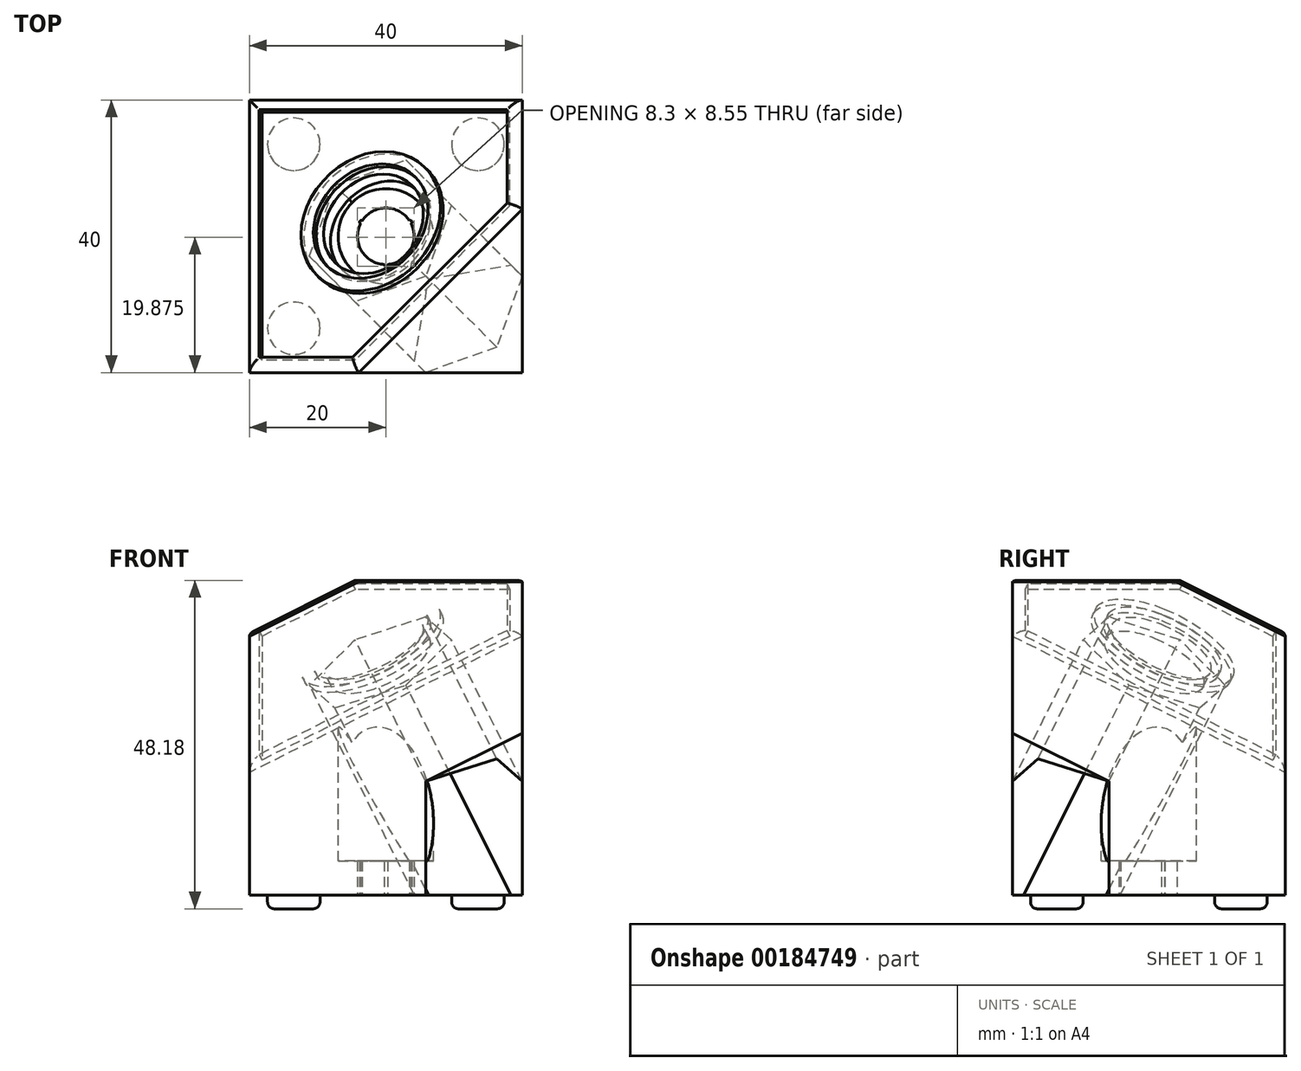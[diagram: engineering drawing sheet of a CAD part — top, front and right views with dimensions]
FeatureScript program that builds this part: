
annotation { "Feature Type Name" : "Feature", "Feature Type Description" : "" }
export const myFeature = defineFeature(function(context is Context, id is Id, definition is map)
    precondition{}
    {
        {
            var Q0;
            Q0=qCreatedBy(makeId("Top.planeOp"),FACE);
            var sketch = newSketch(context, id + "F0", { "sketchPlane" : qUnion([Q0])});
            skLineSegment(sketch, "E0.bottom", {"start": v(20, -20) * mm, "end": v(-20, -20) * mm});
            skLineSegment(sketch, "E0.top", {"start": v(20, 20) * mm, "end": v(-20, 20) * mm});
            skLineSegment(sketch, "E0.left", {"start": v(20, -20) * mm, "end": v(20, 20) * mm});
            skLineSegment(sketch, "E0.right", {"start": v(-20, -20) * mm, "end": v(-20, 20) * mm});
            skPoint(sketch, "E0.middle", {"position": v(0, 0) * mm});
            skSolve(sketch);
        }
        {
            var Q0;
            Q0=makeQuery(id+"F0.imprint","IMPRINT",FACE,{"disambiguationData":[TD([[makeQuery(id+"F0.imprint","IMPRINT",EDGE,{"derivedFrom":sQuery(id+"F0.wireOp",EDGE,"E0.bottom")}),-1.0]])]});
            extrude(context, id + "F1", {"entities" : qUnion([Q0]), "depth" : 20 * mm});
        }
        {
            var Q0;
            Q0=makeQuery(id+"F1.opExtrude","CAP_VERTEX",VERTEX,{"disambiguationData":[OSD([sQuery(id+"F0.wireOp",EDGE,"E0.top"),sQuery(id+"F0.wireOp",EDGE,"E0.left")])],"isStart":false});
            var Q1;
            Q1=makeQuery(id+"F1.opExtrude","CAP_VERTEX",VERTEX,{"disambiguationData":[OSD([sQuery(id+"F0.wireOp",EDGE,"E0.bottom"),sQuery(id+"F0.wireOp",EDGE,"E0.right")])],"isStart":false});
            var Q2;
            Q2=makeQuery(id+"F1.opExtrude","CAP_VERTEX",VERTEX,{"disambiguationData":[OSD([sQuery(id+"F0.wireOp",EDGE,"E0.top"),sQuery(id+"F0.wireOp",EDGE,"E0.right")])],"isStart":true});
            cPlane(context, id + "F2", {"entities" : qUnion([Q0, Q1, Q2]), "cplaneType" : CPlaneType.THREE_POINT, "offset" : 25 * mm, "width" : 150 * mm, "height" : 150 * mm});
        }
        {
            var Q0;
            Q0=makeQuery(id+"F1.opExtrude","CAP_FACE",FACE,{"disambiguationData":[OSD([sQuery(id+"F0.wireOp",EDGE,"E0.bottom"),sQuery(id+"F0.wireOp",EDGE,"E0.top"),sQuery(id+"F0.wireOp",EDGE,"E0.left"),sQuery(id+"F0.wireOp",EDGE,"E0.right")])],"isStart":true});
            extrude(context, id + "F3", {"entities" : qUnion([Q0]), "operationType" : NewBodyOperationType.ADD, "depth" : 18 * mm});
        }
        {
            var Q0;
            Q0=makeQuery(id+"F1.opExtrude","CAP_FACE",FACE,{"disambiguationData":[OSD([sQuery(id+"F0.wireOp",EDGE,"E0.bottom"),sQuery(id+"F0.wireOp",EDGE,"E0.top"),sQuery(id+"F0.wireOp",EDGE,"E0.left"),sQuery(id+"F0.wireOp",EDGE,"E0.right")])],"isStart":false});
            extrude(context, id + "F4", {"entities" : qUnion([Q0]), "operationType" : NewBodyOperationType.ADD, "depth" : 8 * mm});
        }
        {
            var Q0;
            Q0=qCreatedBy(id+"F2.planeOp",FACE);
            var sketch = newSketch(context, id + "F5", { "sketchPlane" : qUnion([Q0])});
            skCircle(sketch, "E1", {"center": v(2.39, -7.49) * mm, "radius": 48.4 * mm});
            skSolve(sketch);
        }
        {
            var Q0;
            Q0=makeQuery(id+"F5.imprint","IMPRINT",FACE,{"disambiguationData":[TD([[makeQuery(id+"F5.imprint","IMPRINT",EDGE,{"derivedFrom":sQuery(id+"F5.wireOp",EDGE,"E1")}),1.0]])]});
            extrude(context, id + "F6", {"entities" : qUnion([Q0]), "operationType" : NewBodyOperationType.REMOVE, "depth" : 25 * mm});
        }
        {
            var Q0;
            Q0=makeQuery(id+"F6.boolean.opBoolean","COPY",FACE,{"derivedFrom":makeQuery(id+"F6.opExtrude","CAP_FACE",FACE,{"disambiguationData":[OSD([sQuery(id+"F5.wireOp",EDGE,"E1")])],"isStart":true})});
            var sketch = newSketch(context, id + "F7", { "sketchPlane" : qUnion([Q0])});
            skLineSegment(sketch, "E2", {"start": v(16.07, -19.68) * mm, "end": v(-14.6, 17.89) * mm, "construction": true});
            skCircle(sketch, "E3", {"center": v(5.31, -6.5) * mm, "radius": 8 * mm});
            skSolve(sketch);
        }
        {
            var Q0;
            Q0=makeQuery(id+"F7.imprint","IMPRINT",FACE,{"disambiguationData":[TD([[makeQuery(id+"F7.imprint","IMPRINT",EDGE,{"derivedFrom":sQuery(id+"F7.wireOp",EDGE,"E3")}),1.0]])]});
            extrude(context, id + "F8", {"entities" : qUnion([Q0]), "operationType" : NewBodyOperationType.REMOVE, "endBound" : BoundingType.THROUGH_ALL, "oppositeDirection" : true, "depth" : 25 * mm});
        }
        {
            var Q0;
            Q0=qCreatedBy(id+"F2.planeOp",FACE);
            cPlane(context, id + "F9", {"entities" : qUnion([Q0]), "cplaneType" : CPlaneType.OFFSET, "offset" : 40 * mm, "oppositeDirection" : true, "width" : 150 * mm, "height" : 150 * mm});
        }
        {
            var Q0;
            Q0=qCreatedBy(id+"F9.planeOp",FACE);
            var sketch = newSketch(context, id + "F10", { "sketchPlane" : qUnion([Q0])});
            skArc(sketch, "E4.0", {"start": v(10.03, -0.05) * mm, "mid": v(0.26, -0.31) * mm, "end": v(-1.96, -9.84) * mm, "construction": true});
            skArc(sketch, "E5.0", {"start": v(10.37, -12.7) * mm, "mid": v(3.5, -14.3) * mm, "end": v(-1.96, -9.84) * mm, "construction": true});
            skArc(sketch, "E6.0", {"start": v(10.37, -12.7) * mm, "mid": v(13.31, -6.3) * mm, "end": v(10.03, -0.05) * mm, "construction": true});
            skCircle(sketch, "E7.cCircle", {"center": v(5.31, -6.5) * mm, "radius": 10 * mm, "construction": true});
            skLineSegment(sketch, "E7.0", {"start": v(9.4, 4.29) * mm, "end": v(16.71, -4.66) * mm});
            skLineSegment(sketch, "E7.1", {"start": v(16.71, -4.66) * mm, "end": v(12.62, -15.45) * mm});
            skLineSegment(sketch, "E7.2", {"start": v(12.62, -15.45) * mm, "end": v(1.22, -17.3) * mm});
            skLineSegment(sketch, "E7.3", {"start": v(1.22, -17.3) * mm, "end": v(-6.08, -8.36) * mm});
            skLineSegment(sketch, "E7.4", {"start": v(-6.08, -8.36) * mm, "end": v(-1.99, 2.44) * mm});
            skLineSegment(sketch, "E7.5", {"start": v(-1.99, 2.44) * mm, "end": v(9.4, 4.29) * mm});
            skPoint(sketch, "E7.0.midPoint", {"position": v(13.06, -0.18) * mm});
            skLineSegment(sketch, "E8.0", {"start": v(24.83, -30.41) * mm, "end": v(10.37, -12.7) * mm, "construction": true});
            skLineSegment(sketch, "E9", {"start": v(-18.46, -33.37) * mm, "end": v(44.1, 17.7) * mm});
            skLineSegment(sketch, "E10", {"start": v(44.1, 17.7) * mm, "end": v(61.04, -3.05) * mm});
            skLineSegment(sketch, "E11", {"start": v(61.04, -3.05) * mm, "end": v(-1.51, -54.13) * mm});
            skLineSegment(sketch, "E12", {"start": v(-1.51, -54.13) * mm, "end": v(-18.46, -33.37) * mm});
            skSolve(sketch);
        }
        {
            var Q0;
            Q0=makeQuery(id+"F10.imprint","IMPRINT",FACE,{"disambiguationData":[TD([[makeQuery(id+"F10.imprint","IMPRINT",EDGE,{"derivedFrom":sQuery(id+"F10.wireOp",EDGE,"E7.0")}),-1.0]])]});
            var Q1;
            {var subQ0=sQuery(id+"F10.wireOp",EDGE,"E7.2");Q1=makeQuery(id+"F10.imprint","IMPRINT",FACE,{"disambiguationData":[TD([[makeQuery(id+"F10.imprint","IMPRINT",EDGE,{"derivedFrom":subQ0}),-1.0]])]});}
            extrude(context, id + "F11", {"entities" : qUnion([Q0, Q1]), "operationType" : NewBodyOperationType.REMOVE, "endBound" : BoundingType.SYMMETRIC, "oppositeDirection" : true, "depth" : 75 * mm});
        }
        {
            var Q0;
            {var subQ1=sQuery(id+"F10.wireOp",EDGE,"E7.1");Q0=makeQuery(id+"F10.imprint","IMPRINT",FACE,{"disambiguationData":[TD([[makeQuery(id+"F10.imprint","IMPRINT",EDGE,{"derivedFrom":subQ1}),1.0]])]});}
            extrude(context, id + "F12", {"entities" : qUnion([Q0]), "operationType" : NewBodyOperationType.REMOVE, "depth" : 12.05 * mm});
        }
        {
            var Q0;
            Q0=makeQuery(id+"F3.opExtrude","CAP_FACE",FACE,{"disambiguationData":[OSD([sQuery(id+"F0.wireOp",EDGE,"E0.bottom"),sQuery(id+"F0.wireOp",EDGE,"E0.top"),sQuery(id+"F0.wireOp",EDGE,"E0.left"),sQuery(id+"F0.wireOp",EDGE,"E0.right")])],"isStart":false});
            var sketch = newSketch(context, id + "F13", { "sketchPlane" : qUnion([Q0])});
            skArc(sketch, "E13", {"start": v(-0.25, 4.14) * mm, "mid": v(-3.6, 2.08) * mm, "end": v(-3.71, -1.85) * mm});
            skArc(sketch, "E14", {"start": v(0.25, 4.14) * mm, "mid": v(0, 4.4) * mm, "end": v(-0.25, 4.14) * mm});
            skArc(sketch, "E15.1.0", {"start": v(-3.71, -1.85) * mm, "mid": v(-3.81, -2.2) * mm, "end": v(-3.46, -2.29) * mm});
            skArc(sketch, "E15.2.0", {"start": v(3.46, -2.29) * mm, "mid": v(3.81, -2.2) * mm, "end": v(3.71, -1.85) * mm});
            skArc(sketch, "E16.trimOffspring", {"start": v(3.71, -1.85) * mm, "mid": v(3.6, 2.08) * mm, "end": v(0.25, 4.14) * mm});
            skArc(sketch, "E17.trimOffspring", {"start": v(-3.46, -2.29) * mm, "mid": v(0, -4.15) * mm, "end": v(3.46, -2.29) * mm});
            skCircle(sketch, "E18", {"center": v(-13.5, 13.5) * mm, "radius": 3.85 * mm});
            skCircle(sketch, "E19.1.0", {"center": v(-13.5, -13.5) * mm, "radius": 3.85 * mm});
            skCircle(sketch, "E19.2.0", {"center": v(13.5, -13.5) * mm, "radius": 3.85 * mm});
            skCircle(sketch, "E19.3.0", {"center": v(13.5, 13.5) * mm, "radius": 3.85 * mm});
            skLineSegment(sketch, "E20.rect.bottom", {"start": v(19, -20) * mm, "end": v(-19, -20) * mm});
            skLineSegment(sketch, "E20.rect.top", {"start": v(19, 20) * mm, "end": v(4.2, 20) * mm});
            skLineSegment(sketch, "E20.rect.left", {"start": v(20, -19) * mm, "end": v(20, 19) * mm});
            skLineSegment(sketch, "E20.rect.right", {"start": v(-20, -19) * mm, "end": v(-20, 19) * mm});
            skPoint(sketch, "E21.visualSharp", {"position": v(-20, 20) * mm});
            skArc(sketch, "E21.filletArc", {"start": v(-19, 20) * mm, "mid": v(-19.7, 19.7) * mm, "end": v(-20, 19) * mm});
            skPoint(sketch, "E22.visualSharp", {"position": v(20, 20) * mm});
            skArc(sketch, "E22.filletArc", {"start": v(20, 19) * mm, "mid": v(19.7, 19.7) * mm, "end": v(19, 20) * mm});
            skPoint(sketch, "E23.visualSharp", {"position": v(-20, -20) * mm});
            skArc(sketch, "E23.filletArc", {"start": v(-20, -19) * mm, "mid": v(-19.7, -19.7) * mm, "end": v(-19, -20) * mm});
            skPoint(sketch, "E24.visualSharp", {"position": v(20, -20) * mm});
            skArc(sketch, "E24.filletArc", {"start": v(19, -20) * mm, "mid": v(19.7, -19.7) * mm, "end": v(20, -19) * mm});
            skLineSegment(sketch, "E25.rect.bottom", {"start": v(-16, -4.2) * mm, "end": v(-20, -4.2) * mm});
            skLineSegment(sketch, "E25.rect.top", {"start": v(-16, 4.2) * mm, "end": v(-20, 4.2) * mm});
            skLineSegment(sketch, "E25.rect.right", {"start": v(-20, -4.2) * mm, "end": v(-20, 4.2) * mm});
            skPoint(sketch, "E25.rect.middle", {"position": v(-18, 0) * mm});
            skLineSegment(sketch, "E26.rect.bottom", {"start": v(-16, 7.25) * mm, "end": v(-9.36, 7.25) * mm});
            skLineSegment(sketch, "E26.rect.top", {"start": v(-16, -7.25) * mm, "end": v(-9.36, -7.25) * mm});
            skLineSegment(sketch, "E26.rect.left", {"start": v(-16, 7.25) * mm, "end": v(-16, 4.2) * mm});
            skPoint(sketch, "E26.rect.middle", {"position": v(-12.68, 0) * mm});
            skPoint(sketch, "E26.rect.middle.positionSnap0", {"position": v(-16, 0) * mm});
            skPoint(sketch, "E26.rect.cornerSnap0", {"position": v(-16, 0) * mm});
            skPoint(sketch, "E26.rect.centerSnap0", {"position": v(-16, 0) * mm});
            skLineSegment(sketch, "E27.trimOffspring", {"start": v(-16, -4.2) * mm, "end": v(-16, -7.25) * mm});
            skArc(sketch, "E28", {"start": v(-9.36, 7.25) * mm, "mid": v(-6, 0) * mm, "end": v(-9.36, -7.25) * mm});
            skLineSegment(sketch, "E29.1.0", {"start": v(4.2, -16) * mm, "end": v(7.25, -16) * mm});
            skLineSegment(sketch, "E29.1.1", {"start": v(4.2, -16) * mm, "end": v(4.2, -20) * mm});
            skPoint(sketch, "E29.1.2", {"position": v(0, -16) * mm});
            skLineSegment(sketch, "E29.1.3", {"start": v(-7.25, -16) * mm, "end": v(-4.2, -16) * mm});
            skPoint(sketch, "E29.1.4", {"position": v(0, -18) * mm});
            skLineSegment(sketch, "E29.1.5", {"start": v(7.25, -16) * mm, "end": v(7.25, -9.36) * mm});
            skArc(sketch, "E29.1.6", {"start": v(-7.25, -9.36) * mm, "mid": v(0, -6) * mm, "end": v(7.25, -9.36) * mm});
            skLineSegment(sketch, "E29.1.7", {"start": v(-7.25, -16) * mm, "end": v(-7.25, -9.36) * mm});
            skLineSegment(sketch, "E29.1.8", {"start": v(4.2, -20) * mm, "end": v(-4.2, -20) * mm});
            skLineSegment(sketch, "E29.1.9", {"start": v(-4.2, -16) * mm, "end": v(-4.2, -20) * mm});
            skPoint(sketch, "E29.1.10", {"position": v(0, -12.68) * mm});
            skPoint(sketch, "E29.1.11", {"position": v(0, -16) * mm});
            skPoint(sketch, "E29.1.12", {"position": v(0, -16) * mm});
            skLineSegment(sketch, "E29.2.0", {"start": v(16, 4.2) * mm, "end": v(16, 7.25) * mm});
            skLineSegment(sketch, "E29.2.1", {"start": v(16, 4.2) * mm, "end": v(20, 4.2) * mm});
            skPoint(sketch, "E29.2.2", {"position": v(16, 0) * mm});
            skLineSegment(sketch, "E29.2.3", {"start": v(16, -7.25) * mm, "end": v(16, -4.2) * mm});
            skPoint(sketch, "E29.2.4", {"position": v(18, 0) * mm});
            skLineSegment(sketch, "E29.2.5", {"start": v(16, 7.25) * mm, "end": v(9.36, 7.25) * mm});
            skArc(sketch, "E29.2.6", {"start": v(9.36, -7.25) * mm, "mid": v(6, 0) * mm, "end": v(9.36, 7.25) * mm});
            skLineSegment(sketch, "E29.2.7", {"start": v(16, -7.25) * mm, "end": v(9.36, -7.25) * mm});
            skLineSegment(sketch, "E29.2.8", {"start": v(20, 4.2) * mm, "end": v(20, -4.2) * mm});
            skLineSegment(sketch, "E29.2.9", {"start": v(16, -4.2) * mm, "end": v(20, -4.2) * mm});
            skPoint(sketch, "E29.2.10", {"position": v(12.68, 0) * mm});
            skPoint(sketch, "E29.2.11", {"position": v(16, 0) * mm});
            skPoint(sketch, "E29.2.12", {"position": v(16, 0) * mm});
            skLineSegment(sketch, "E29.3.0", {"start": v(-4.2, 16) * mm, "end": v(-7.25, 16) * mm});
            skLineSegment(sketch, "E29.3.1", {"start": v(-4.2, 16) * mm, "end": v(-4.2, 20) * mm});
            skPoint(sketch, "E29.3.2", {"position": v(0, 16) * mm});
            skLineSegment(sketch, "E29.3.3", {"start": v(7.25, 16) * mm, "end": v(4.2, 16) * mm});
            skPoint(sketch, "E29.3.4", {"position": v(0, 18) * mm});
            skLineSegment(sketch, "E29.3.5", {"start": v(-7.25, 16) * mm, "end": v(-7.25, 9.36) * mm});
            skArc(sketch, "E29.3.6", {"start": v(7.25, 9.36) * mm, "mid": v(0, 6) * mm, "end": v(-7.25, 9.36) * mm});
            skLineSegment(sketch, "E29.3.7", {"start": v(7.25, 16) * mm, "end": v(7.25, 9.36) * mm});
            skLineSegment(sketch, "E29.3.8", {"start": v(-4.2, 20) * mm, "end": v(4.2, 20) * mm});
            skLineSegment(sketch, "E29.3.9", {"start": v(4.2, 16) * mm, "end": v(4.2, 20) * mm});
            skPoint(sketch, "E29.3.10", {"position": v(0, 12.68) * mm});
            skPoint(sketch, "E29.3.11", {"position": v(0, 16) * mm});
            skPoint(sketch, "E29.3.12", {"position": v(0, 16) * mm});
            skLineSegment(sketch, "E30.trimOffspring", {"start": v(-4.2, 20) * mm, "end": v(-19, 20) * mm});
            skSolve(sketch);
        }
        {
            var Q0;
            Q0=makeQuery(id+"F13.imprint","IMPRINT",FACE,{"disambiguationData":[TD([[makeQuery(id+"F13.imprint","IMPRINT",EDGE,{"derivedFrom":sQuery(id+"F13.wireOp",EDGE,"E18")}),1.0]])]});
            var Q1;
            Q1=makeQuery(id+"F13.imprint","IMPRINT",FACE,{"disambiguationData":[TD([[makeQuery(id+"F13.imprint","IMPRINT",EDGE,{"derivedFrom":sQuery(id+"F13.wireOp",EDGE,"E19.1.0")}),1.0]])]});
            var Q2;
            Q2=makeQuery(id+"F13.imprint","IMPRINT",FACE,{"disambiguationData":[TD([[makeQuery(id+"F13.imprint","IMPRINT",EDGE,{"derivedFrom":sQuery(id+"F13.wireOp",EDGE,"E19.2.0")}),1.0]])]});
            extrude(context, id + "F14", {"entities" : qUnion([Q0, Q1, Q2]), "operationType" : NewBodyOperationType.ADD, "depth" : 2 * mm});
        }
        {
            var Q0;
            Q0=makeQuery(id+"F13.imprint","IMPRINT",FACE,{"disambiguationData":[TD([[makeQuery(id+"F13.imprint","IMPRINT",EDGE,{"derivedFrom":sQuery(id+"F13.wireOp",EDGE,"E13")}),1.0]])]});
            extrude(context, id + "F15", {"entities" : qUnion([Q0]), "operationType" : NewBodyOperationType.REMOVE, "oppositeDirection" : true, "depth" : 25 * mm});
        }
        {
            var Q0;
            Q0=qCreatedBy(makeId("Top.planeOp"),FACE);
            var sketch = newSketch(context, id + "F16", { "sketchPlane" : qUnion([Q0])});
            skCircle(sketch, "E31", {"center": v(0, 0) * mm, "radius": 7 * mm});
            skSolve(sketch);
        }
        {
            var Q0;
            Q0=makeQuery(id+"F16.imprint","IMPRINT",FACE,{"disambiguationData":[TD([[makeQuery(id+"F16.imprint","IMPRINT",EDGE,{"derivedFrom":sQuery(id+"F16.wireOp",EDGE,"E31")}),1.0]])]});
            extrude(context, id + "F17", {"entities" : qUnion([Q0]), "operationType" : NewBodyOperationType.REMOVE, "oppositeDirection" : true, "depth" : 13 * mm});
        }
        {
            var Q0;
            Q0=makeQuery(id+"F16.imprint","IMPRINT",FACE,{"disambiguationData":[TD([[makeQuery(id+"F16.imprint","IMPRINT",EDGE,{"derivedFrom":sQuery(id+"F16.wireOp",EDGE,"E31")}),1.0]])]});
            extrude(context, id + "F18", {"entities" : qUnion([Q0]), "operationType" : NewBodyOperationType.REMOVE, "depth" : 18.5 * mm});
        }
        {
            var Q0;
            Q0=makeQuery(id+"F14.opExtrude","CAP_EDGE",EDGE,{"disambiguationData":[OSD([sQuery(id+"F13.wireOp",EDGE,"E19.1.0")])],"isStart":false});
            var Q1;
            Q1=makeQuery(id+"F14.opExtrude","CAP_EDGE",EDGE,{"disambiguationData":[OSD([sQuery(id+"F13.wireOp",EDGE,"E18")])],"isStart":false});
            var Q2;
            Q2=makeQuery(id+"F14.opExtrude","CAP_EDGE",EDGE,{"disambiguationData":[OSD([sQuery(id+"F13.wireOp",EDGE,"E19.2.0")])],"isStart":false});
            fillet(context, id + "F19", {"entities" : qUnion([Q0, Q1, Q2]), "radius" : 1 * mm, "tangentPropagation" : true, "allowEdgeOverflow" : false});
        }
        {
            var Q0;
            Q0=makeQuery(id+"F6.boolean.opBoolean","COPY",FACE,{"derivedFrom":makeQuery(id+"F6.opExtrude","CAP_FACE",FACE,{"disambiguationData":[OSD([sQuery(id+"F5.wireOp",EDGE,"E1")])],"isStart":true})});
            var sketch = newSketch(context, id + "F20", { "sketchPlane" : qUnion([Q0])});
            skLineSegment(sketch, "E32.0", {"start": v(29.21, -8.94) * mm, "end": v(29.21, 8.94) * mm});
            skLineSegment(sketch, "E33.0", {"start": v(29.21, -8.94) * mm, "end": v(2.92, -30.41) * mm});
            skLineSegment(sketch, "E34.0", {"start": v(2.92, -30.41) * mm, "end": v(-14.6, -26.83) * mm});
            skLineSegment(sketch, "E35.0", {"start": v(-14.6, -26.83) * mm, "end": v(-14.6, 17.89) * mm});
            skLineSegment(sketch, "E36.0", {"start": v(29.21, 8.94) * mm, "end": v(-14.6, 17.89) * mm});
            skLineSegment(sketch, "E37.0", {"start": v(2.4, -28.26) * mm, "end": v(-12.6, -25.2) * mm});
            skLineSegment(sketch, "E37.1", {"start": v(27.21, -8) * mm, "end": v(2.4, -28.26) * mm});
            skLineSegment(sketch, "E37.2", {"start": v(-12.6, -25.2) * mm, "end": v(-12.6, 15.44) * mm});
            skLineSegment(sketch, "E37.3", {"start": v(27.21, 7.31) * mm, "end": v(-12.6, 15.44) * mm});
            skLineSegment(sketch, "E37.4", {"start": v(27.21, -8) * mm, "end": v(27.21, 7.31) * mm});
            skCircle(sketch, "E38", {"center": v(5.31, -6.5) * mm, "radius": 9.2 * mm});
            skCircle(sketch, "E39.0", {"center": v(5.31, -6.5) * mm, "radius": 11.2 * mm});
            skSolve(sketch);
        }
        {
            var Q0;
            Q0=makeQuery(id+"F20.imprint","IMPRINT",FACE,{"disambiguationData":[TD([[makeQuery(id+"F20.imprint","IMPRINT",EDGE,{"derivedFrom":sQuery(id+"F20.wireOp",EDGE,"E32.0")}),1.0]])]});
            var Q1;
            Q1=makeQuery(id+"F20.imprint","IMPRINT",FACE,{"disambiguationData":[TD([[makeQuery(id+"F20.imprint","IMPRINT",EDGE,{"derivedFrom":sQuery(id+"F20.wireOp",EDGE,"E38")}),-1.0]])]});
            extrude(context, id + "F21", {"entities" : qUnion([Q0, Q1]), "operationType" : NewBodyOperationType.ADD, "depth" : 1 * mm});
        }
        {
            var Q0;
            Q0=makeQuery(id+"F21.opExtrude","CAP_EDGE",EDGE,{"disambiguationData":[OSD([sQuery(id+"F20.wireOp",EDGE,"E34.0")])],"isStart":false});
            var Q1;
            Q1=makeQuery(id+"F21.opExtrude","CAP_EDGE",EDGE,{"disambiguationData":[OSD([sQuery(id+"F20.wireOp",EDGE,"E35.0")])],"isStart":false});
            var Q2;
            Q2=makeQuery(id+"F21.opExtrude","CAP_EDGE",EDGE,{"disambiguationData":[OSD([sQuery(id+"F20.wireOp",EDGE,"E36.0")])],"isStart":false});
            var Q3;
            Q3=makeQuery(id+"F21.opExtrude","CAP_EDGE",EDGE,{"disambiguationData":[OSD([sQuery(id+"F20.wireOp",EDGE,"E32.0")])],"isStart":false});
            var Q4;
            Q4=makeQuery(id+"F21.opExtrude","CAP_EDGE",EDGE,{"disambiguationData":[OSD([sQuery(id+"F20.wireOp",EDGE,"E33.0")])],"isStart":false});
            fillet(context, id + "F22", {"entities" : qUnion([Q0, Q1, Q2, Q3, Q4]), "radius" : 2 * mm, "tangentPropagation" : true, "allowEdgeOverflow" : false});
        }
    });
